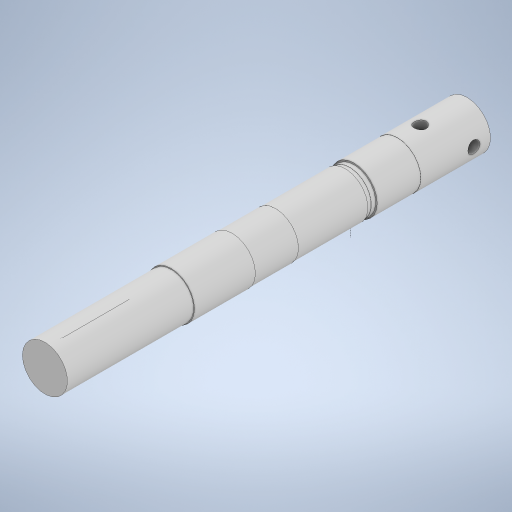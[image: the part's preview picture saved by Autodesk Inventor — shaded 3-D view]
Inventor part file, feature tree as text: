
AUTODESK INVENTOR PART (.ipt)
format: ipt  version: 2024 (Build 280153000, 153)  size: 329,216 bytes
history: native  units: mm
features: sketch x6, extrude x3, plane x1, revolve x1
ambient origin geometry x8: Origin, YZ Plane, XZ Plane, XY Plane, X Axis, Y Axis, Z Axis, Center Point
bodies: Body1 (feature_tree)
feature tree (11):
  sketch  "Sketch1"  dims[d0=105.0mm d3=70.0mm]
  plane  "Work Plane1"
  sketch  "Sketch2"  dims[d2=80.0mm d4=5.0mm]
  sketch  "Sketch3"  dims[d5=5.0mm d6=50.0mm]
  sketch  "Sketch4"  dims[d15=40.0mm d16=50.0mm]
  revolve  "Revolution1"  [1 undecoded]
  extrude  "Extrusion4"  Depth=5.0mm
  extrude  "Extrusion5"  Depth=5.0mm
  extrude  "Extrusion6"  Depth=50.0mm
  sketch  "Sketch5"  dims[d17=15.0mm]
  sketch  "Sketch6"  dims[d18=10.0mm d19=10.0mm d22=14.0mm d28=14.0mm d31=90.0deg d32=10.0mm d33=0.0mm d34=20.0mm d35=45.0mm d36=0.0mm d37=0.0mm d38=35.0mm d39=30.0mm d40=0.0mm d41=0.0mm d65=260.0mm d66=80.0mm d67=115.0mm d68=75.0mm d69=25.85mm d70=26.85mm d71=26.05mm d78=24.85mm d82=5.0mm d83=50.0mm d84=25.05mm d85=26.95mm d86=80.0mm d87=25.85mm d88=26.35mm d89=26.75mm d20=0.5mm d21=0.872665mm d23=0.872665mm]
note: 1 required parameter value undecoded (feature->parameter linkage not recoverable at this tier; creation-order binding heuristic only, values carry confidence <= 0.55)
